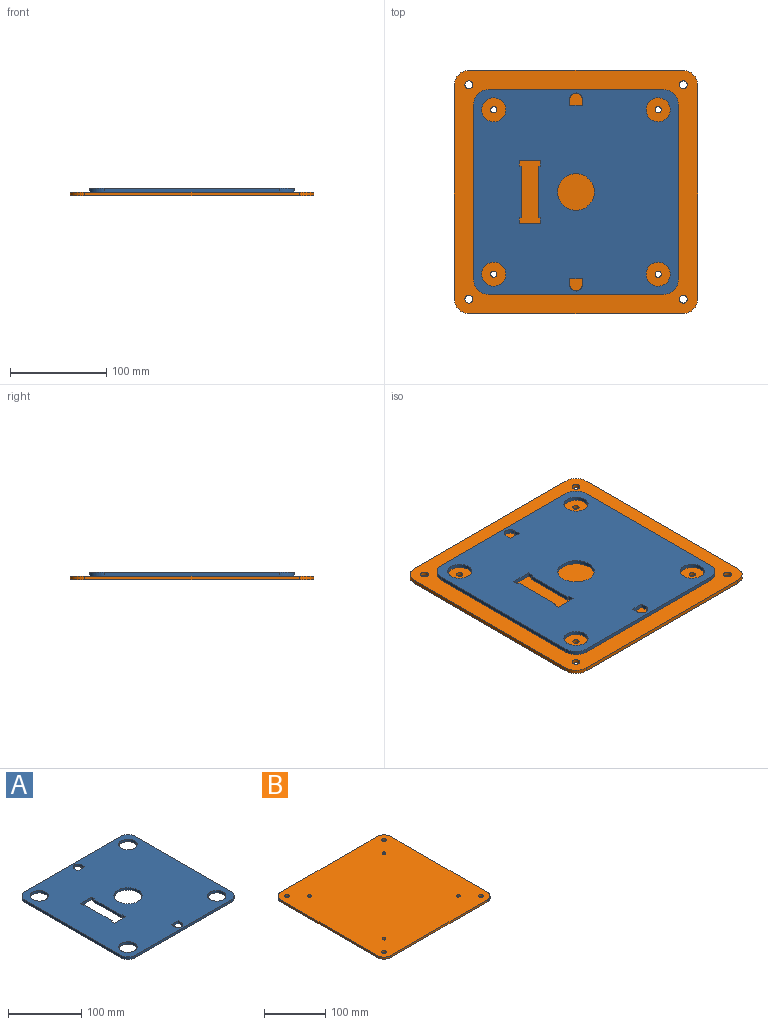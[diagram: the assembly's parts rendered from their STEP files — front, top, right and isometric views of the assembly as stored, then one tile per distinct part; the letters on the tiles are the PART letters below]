
ASSEMBLY  parts=2 mates=1
PART A: 35 faces, bbox 213x213x4 mm
  f0: plane 213x213mm, normal (0,0,1), area 40537.5mm2, adj f2,f3,f4,f5,f6,f7,f8,f9
  f1: plane 213x213mm, normal (0,0,-1), area 40537.5mm2, adj f2,f3,f4,f5,f6,f7,f8,f9
  f2: plane 183x4mm, normal (1,0,0), area 732mm2, adj f0,f1,f3,f9
  f3: cylinder r=15mm len=15mm, axis (0,0,-1), area 94.2mm2, adj f0,f1,f2,f4
  f4: plane 183x4mm, normal (0,1,0), area 732mm2, adj f0,f1,f3,f5
  f5: cylinder r=15mm len=15mm, axis (0,0,-1), area 94.2mm2, adj f0,f1,f4,f6
  f6: plane 183x4mm, normal (-1,0,0), area 732mm2, adj f0,f1,f5,f7
  f7: cylinder r=15mm len=15mm, axis (0,0,-1), area 94.2mm2, adj f0,f1,f6,f8
  f8: plane 183x4mm, normal (0,-1,0), area 732mm2, adj f0,f1,f7,f9
  f9: cylinder r=15mm len=15mm, axis (0,0,-1), area 94.2mm2, adj f0,f1,f2,f8
  f10: cylinder r=12.5mm len=25mm, axis (0,0,1), area 314.2mm2, adj f0,f1
  f11: plane 6x4mm, normal (1,0,0), area 24mm2, adj f0,f1,f12,f22
  f12: plane 22x4mm, normal (0,1,0), area 88mm2, adj f0,f1,f11,f13
  f13: plane 6x4mm, normal (-1,0,0), area 24mm2, adj f0,f1,f12,f14
  f14: plane 4x2mm, normal (0,-1,0), area 8mm2, adj f0,f1,f13,f15
  f15: plane 53.5x4mm, normal (-1,0,0), area 214mm2, adj f0,f1,f14,f16
  f16: plane 4x2mm, normal (0,1,0), area 8mm2, adj f0,f1,f15,f17
  f17: plane 6x4mm, normal (-1,0,0), area 24mm2, adj f0,f1,f16,f18
  f18: plane 22x4mm, normal (0,-1,0), area 88mm2, adj f0,f1,f17,f19
  f19: plane 6x4mm, normal (1,0,0), area 24mm2, adj f0,f1,f18,f20
  f20: plane 4x2mm, normal (0,1,0), area 8mm2, adj f0,f1,f19,f21
  f21: plane 53.5x4mm, normal (1,0,0), area 214mm2, adj f0,f1,f20,f22
  f22: plane 4x2mm, normal (0,-1,0), area 8mm2, adj f0,f1,f11,f21
  f23: cylinder r=19.1mm len=38.2mm, axis (0,0,1), area 480mm2, adj f0,f1
  f24: cylinder r=6.5mm len=13mm, axis (0,0,1), area 81.7mm2, adj f0,f1,f25,f27
  f25: plane 6.5x4mm, normal (-1,0,0), area 26mm2, adj f0,f1,f24,f26
  f26: plane 13x4mm, normal (0,-1,0), area 52mm2, adj f0,f1,f25,f27
  f27: plane 6.5x4mm, normal (1,0,0), area 26mm2, adj f0,f1,f24,f26
  f28: plane 13x4mm, normal (0,1,0), area 52mm2, adj f0,f1,f29,f31
  f29: plane 6.5x4mm, normal (-1,0,0), area 26mm2, adj f0,f1,f28,f30
  f30: cylinder r=6.5mm len=13mm, axis (0,0,1), area 81.7mm2, adj f0,f1,f29,f31
  f31: plane 6.5x4mm, normal (1,0,0), area 26mm2, adj f0,f1,f28,f30
  f32: cylinder r=12.5mm len=25mm, axis (0,0,1), area 314.2mm2, adj f0,f1
  f33: cylinder r=12.5mm len=25mm, axis (0,0,1), area 314.2mm2, adj f0,f1
  f34: cylinder r=12.5mm len=25mm, axis (0,0,1), area 314.2mm2, adj f0,f1
PART B: 18 faces, bbox 253x253x4 mm
  f0: plane 253x253mm, normal (0,0,1), area 63471.9mm2, adj f2,f3,f4,f5,f6,f7,f8,f9
  f1: plane 253x253mm, normal (0,0,-1), area 63471.9mm2, adj f2,f3,f4,f5,f6,f7,f8,f9
  f2: plane 223x4mm, normal (1,0,0), area 892mm2, adj f0,f1,f3,f9
  f3: cylinder r=15mm len=15mm, axis (0,0,-1), area 94.2mm2, adj f0,f1,f2,f4
  f4: plane 223x4mm, normal (0,1,0), area 892mm2, adj f0,f1,f3,f5
  f5: cylinder r=15mm len=15mm, axis (0,0,-1), area 94.2mm2, adj f0,f1,f4,f6
  f6: plane 223x4mm, normal (-1,0,0), area 892mm2, adj f0,f1,f5,f7
  f7: cylinder r=15mm len=15mm, axis (0,0,-1), area 94.2mm2, adj f0,f1,f6,f8
  f8: plane 223x4mm, normal (0,-1,0), area 892mm2, adj f0,f1,f7,f9
  f9: cylinder r=15mm len=15mm, axis (0,0,-1), area 94.2mm2, adj f0,f1,f2,f8
  f10: cylinder r=3.25mm len=6.5mm, axis (0,0,1), area 81.7mm2, adj f0,f1
  f11: cylinder r=4.1mm len=8.2mm, axis (0,0,1), area 103mm2, adj f0,f1
  f12: cylinder r=4.1mm len=8.2mm, axis (0,0,1), area 103mm2, adj f0,f1
  f13: cylinder r=4.1mm len=8.2mm, axis (0,0,1), area 103mm2, adj f0,f1
  f14: cylinder r=3.25mm len=6.5mm, axis (0,0,1), area 81.7mm2, adj f0,f1
  f15: cylinder r=3.25mm len=6.5mm, axis (0,0,1), area 81.7mm2, adj f0,f1
  f16: cylinder r=3.25mm len=6.5mm, axis (0,0,1), area 81.7mm2, adj f0,f1
  f17: cylinder r=4.1mm len=8.2mm, axis (0,0,1), area 103mm2, adj f0,f1
PLACE A t=(-25.63,-14.93,25)mm
PLACE B t=(-25.63,-14.93,21)mm
MATE fastened B.f16 <-> A.f32  axis (0,0,1) through (-111.13,-100.43,25)mm
